# Revit family: Shower-Showerhead-KOHLER-Forte-K-10327
name_source: partatom
category: Plumbing Fixtures
revit_build: Autodesk Revit 2015 (Build: 20140606_1530(x64)
units: mm (PartAtom-declared; Revit-internal decimal feet)

## types (13) — shared parameters
ADA Compliant = No
Assembly Code = D2010700
CW Connection = No
Cold Water Inlet = Cold Water Inlet
Date Modified = 02/15/2019
Default Elevation = 0"
Drain Included = No
Flow Rate = 2 GPM
HW Connection = Yes
Height = 4 11/16"
Hot Water Inlet = Hot Water Inlet
Length = 5 1/2"
Manufacturer = KOHLER Co.
MasterFormat 1995 = 15410
MasterFormat 2004 = 22.41.23
Material = Metal Construction
Panel Thickness = 0"
Pressure = 80.00 psi
Product Documentation Link = https://www.us.kohler.com
Product Name = Forte
Product Page URL = http://www.us.kohler.com
Tempered Water Inlet = Tempered Water Inlet
URL = https://www.us.kohler.com
Vent Connection = No
Waste Connection = No
Waste Water Outlet = Waste Water Outlet
WaterSense Certified = Yes
Width = 5 1/2"

## per-type parameters (varying)
| type | Description | Finish | Model | Type |
| 1.75 gpm, CP-Polished Chrome | 1.75 GPM Single-Function Showerhead With Katalyst Air-Induction Technology | Kohler-Metal-CP-Polished_Chrome | K-10327-G-CP | 1 |
| 2.0 gpm, G-Brushed Chrome | 2.0GPM Single-Function Showerhead With Katalyst Air-Induction Technology | Kohler-Metal-G-Brushed_Chrome | K-10327-G | 8 |
| 1.75 gpm, AF-Vibrant French Gold | 1.75 GPM Single-Function Showerhead With Katalyst Air-Induction Technology | Kohler-Metal-AF-Vibrant_French_Gold | K-10327-G-AF | 5 |
| 1.75 gpm, PB-Vibrant Polished Brass | 1.75 GPM Single-Function Showerhead With Katalyst Air-Induction Technology | Kohler-Metal-PB-Vibrant_Polished_Brass | K-10327-G-PB | 3 |
| 1.75 gpm, BN-Vibrant Brushed Nickel | 1.75 GPM Single-Function Showerhead With Katalyst Air-Induction Technology | Kohler-Metal-BN-Vibrant_Brushed_Nickel | K-10327-G-BN | 4 |
| 1.75 gpm, BV-Vibrant Brushed Bronze | 1.75 GPM Single-Function Showerhead With Katalyst Air-Induction Technology | Kohler-Metal-BV-Brushed_Bronze | K-10327-G-BV | 6 |
| 2.0 gpm, 2BZ-Oil-Rubbed Bronze | 2.0GPM Single-Function Showerhead With Katalyst Air-Induction Technology | Kohler-Metal-2BZ-Oil_Rubbed_Bronze | K-10327-2BZ | 13 |
| 2.0 gpm, CP- Polished Chrome | 2.0GPM Single-Function Showerhead With Katalyst Air-Induction Technology | Kohler-Metal-CP-Polished_Chrome | K-10327-CP | 7 |
| 2.0 gpm, PB-Vibrant Polished Brass | 2.0GPM Single-Function Showerhead With Katalyst Air-Induction Technology | Kohler-Metal-PB-Vibrant_Polished_Brass | K-10327-PB | 9 |
| 2.0 gpm, BN-Vibrant Brushed Nickel | 2.0GPM Single-Function Showerhead With Katalyst Air-Induction Technology | Kohler-Metal-BN-Vibrant_Brushed_Nickel | K-10327-BN | 10 |
| 2.0 gpm, AF-Vibrant French Gold | 2.0GPM Single-Function Showerhead With Katalyst Air-Induction Technology | Kohler-Metal-AF-Vibrant_French_Gold | K-10327-AF | 11 |
| 2.0 gpm, BV-Vibrant Brushed Bronze | 2.0GPM Single-Function Showerhead With Katalyst Air-Induction Technology | Kohler-Metal-BV-Brushed_Bronze | K-10327-BV | 12 |
| 1.75 gpm, G-Brushed Chrome | 1.75 GPM Single-Function Showerhead With Katalyst Air-Induction Technology | Kohler-Metal-G-Brushed_Chrome | K-10327-G-G | 2 |

## geometry (parser evidence)
native form markers: Sweep x4
no freeform markers — native parametric forms only
